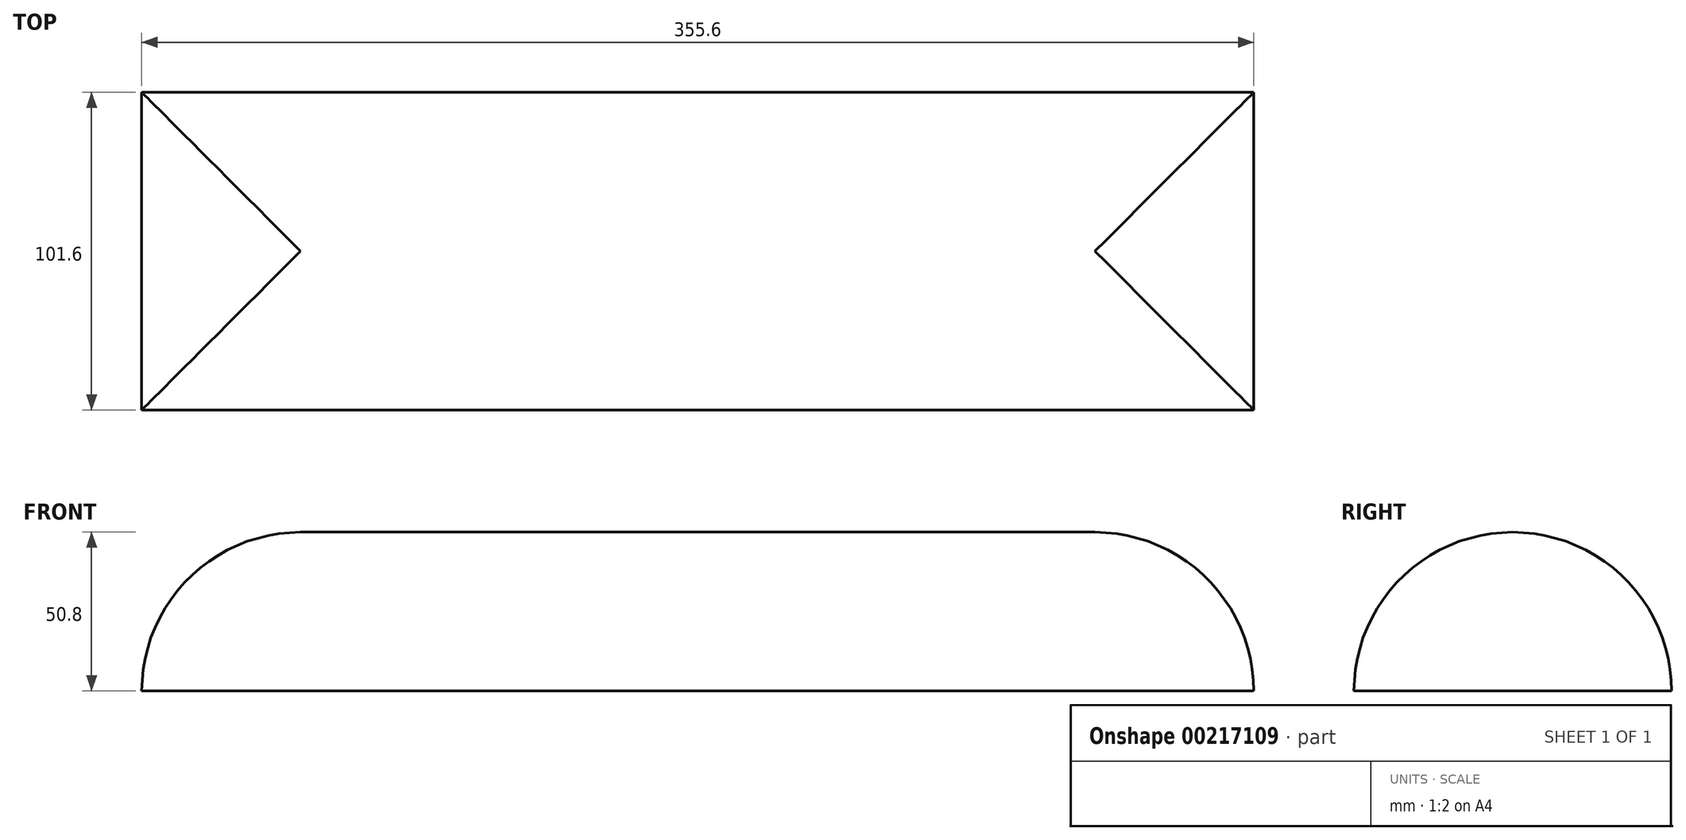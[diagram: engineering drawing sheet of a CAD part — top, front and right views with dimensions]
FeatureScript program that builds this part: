
annotation { "Feature Type Name" : "Feature", "Feature Type Description" : "" }
export const myFeature = defineFeature(function(context is Context, id is Id, definition is map)
    precondition{}
    {
        {
            var Q0;
            Q0=qCreatedBy(makeId("Top.planeOp"),FACE);
            var sketch = newSketch(context, id + "F0", { "sketchPlane" : qUnion([Q0])});
            skLineSegment(sketch, "E0.bottom", {"start": v(177.8, -50.8) * mm, "end": v(-177.8, -50.8) * mm});
            skLineSegment(sketch, "E0.top", {"start": v(177.8, 50.8) * mm, "end": v(-177.8, 50.8) * mm});
            skLineSegment(sketch, "E0.left", {"start": v(177.8, -50.8) * mm, "end": v(177.8, 50.8) * mm});
            skLineSegment(sketch, "E0.right", {"start": v(-177.8, -50.8) * mm, "end": v(-177.8, 50.8) * mm});
            skPoint(sketch, "E0.middle", {"position": v(0, 0) * mm});
            skSolve(sketch);
        }
        {
            var Q0;
            Q0=makeQuery(id+"F0.imprint","IMPRINT",FACE,{"disambiguationData":[TD([[makeQuery(id+"F0.imprint","IMPRINT",EDGE,{"derivedFrom":sQuery(id+"F0.wireOp",EDGE,"E0.bottom")}),-1.0]])]});
            extrude(context, id + "F1", {"entities" : qUnion([Q0]), "depth" : 50.8 * mm});
        }
        {
            var Q0;
            Q0=makeQuery(id+"F1.opExtrude","CAP_EDGE",EDGE,{"disambiguationData":[OSD([sQuery(id+"F0.wireOp",EDGE,"E0.top")])],"isStart":false});
            var Q1;
            Q1=makeQuery(id+"F1.opExtrude","CAP_FACE",FACE,{"disambiguationData":[OSD([sQuery(id+"F0.wireOp",EDGE,"E0.bottom"),sQuery(id+"F0.wireOp",EDGE,"E0.top"),sQuery(id+"F0.wireOp",EDGE,"E0.left"),sQuery(id+"F0.wireOp",EDGE,"E0.right")])],"isStart":false});
            var Q2;
            Q2=makeQuery(id+"F1.opExtrude","CAP_EDGE",EDGE,{"disambiguationData":[OSD([sQuery(id+"F0.wireOp",EDGE,"E0.right")])],"isStart":false});
            var Q3;
            Q3=makeQuery(id+"F1.opExtrude","CAP_EDGE",EDGE,{"disambiguationData":[OSD([sQuery(id+"F0.wireOp",EDGE,"E0.left")])],"isStart":false});
            fillet(context, id + "F2", {"entities" : qUnion([Q0, Q1, Q2, Q3]), "radius" : 50.8 * mm, "tangentPropagation" : true, "allowEdgeOverflow" : false});
        }
    });
